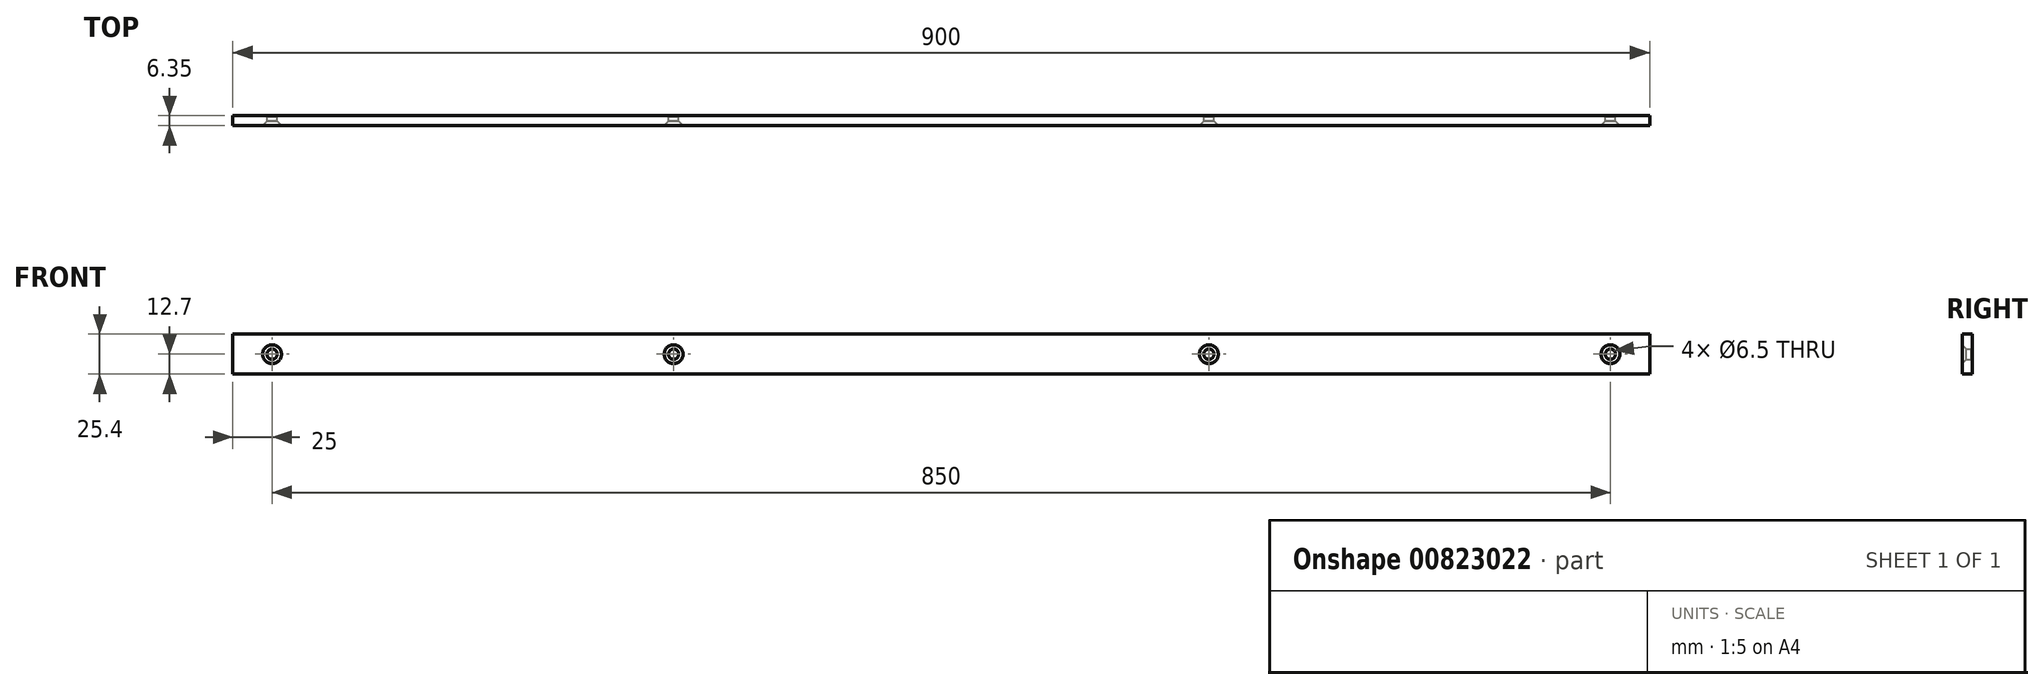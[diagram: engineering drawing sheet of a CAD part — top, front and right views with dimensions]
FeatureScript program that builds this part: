
annotation { "Feature Type Name" : "Feature", "Feature Type Description" : "" }
export const myFeature = defineFeature(function(context is Context, id is Id, definition is map)
    precondition{}
    {
        {
            var Q0;
            Q0=qCreatedBy(makeId("Front.planeOp"),FACE);
            var sketch = newSketch(context, id + "F0", { "sketchPlane" : qUnion([Q0])});
            skLineSegment(sketch, "E0.bottom", {"start": v(450, -12.7) * mm, "end": v(-450, -12.7) * mm});
            skLineSegment(sketch, "E0.top", {"start": v(450, 12.7) * mm, "end": v(-450, 12.7) * mm});
            skLineSegment(sketch, "E0.left", {"start": v(450, -12.7) * mm, "end": v(450, 12.7) * mm});
            skLineSegment(sketch, "E0.right", {"start": v(-450, -12.7) * mm, "end": v(-450, 12.7) * mm});
            skPoint(sketch, "E0.middle", {"position": v(0, 0) * mm});
            skLineSegment(sketch, "E1", {"start": v(0, 0) * mm, "end": v(0, -342.54) * mm, "construction": true});
            skLineSegment(sketch, "E2", {"start": v(0, 0) * mm, "end": v(-425, 0) * mm, "construction": true});
            skLineSegment(sketch, "E3", {"start": v(-425, 0) * mm, "end": v(-425, 337.75) * mm, "construction": true});
            skLineSegment(sketch, "E4", {"start": v(-425, 337.75) * mm, "end": v(-170, 337.75) * mm, "construction": true});
            skLineSegment(sketch, "E5", {"start": v(-170, 337.75) * mm, "end": v(-170, 0) * mm, "construction": true});
            skCircle(sketch, "E6", {"center": v(-425, 0) * mm, "radius": 3.25 * mm});
            skCircle(sketch, "E7", {"center": v(-170, 0) * mm, "radius": 3.25 * mm});
            skCircle(sketch, "E8.MirrorC", {"center": v(170, 0) * mm, "radius": 3.25 * mm});
            skCircle(sketch, "E9.MirrorC", {"center": v(425, 0) * mm, "radius": 3.25 * mm});
            skCircle(sketch, "E10", {"center": v(0, 0) * mm, "radius": 3.25 * mm, "construction": true});
            skSolve(sketch);
        }
        {
            var Q0;
            Q0 = qSketchRegion(id + "F0", true);
            extrude(context, id + "F1", {"entities" : qUnion([Q0]), "depth" : 6.35 * mm, "offsetDistance" : 25 * mm});
        }
        {
            var Q0;
            Q0=makeQuery(id+"F1.opExtrude","CAP_EDGE",EDGE,{"disambiguationData":[OSD([sQuery(id+"F0.wireOp",EDGE,"E6")])],"isStart":false});
            var Q1;
            Q1=makeQuery(id+"F1.opExtrude","CAP_EDGE",EDGE,{"disambiguationData":[OSD([sQuery(id+"F0.wireOp",EDGE,"E7")])],"isStart":false});
            var Q2;
            Q2=makeQuery(id+"F1.opExtrude","CAP_EDGE",EDGE,{"disambiguationData":[OSD([sQuery(id+"F0.wireOp",EDGE,"E10")])],"isStart":false});
            var Q3;
            Q3=makeQuery(id+"F1.opExtrude","CAP_EDGE",EDGE,{"disambiguationData":[OSD([sQuery(id+"F0.wireOp",EDGE,"E8.MirrorC")])],"isStart":false});
            var Q4;
            Q4=makeQuery(id+"F1.opExtrude","CAP_EDGE",EDGE,{"disambiguationData":[OSD([sQuery(id+"F0.wireOp",EDGE,"E9.MirrorC")])],"isStart":false});
            chamfer(context, id + "F2", {"entities" : qUnion([Q0, Q1, Q2, Q3, Q4]), "width" : 2.75 * mm, "tangentPropagation" : true});
        }
        {
            var Q0;
            Q0=makeQuery(id+"F1.opExtrude","CAP_EDGE",EDGE,{"disambiguationData":[OSD([sQuery(id+"F0.wireOp",EDGE,"E9.MirrorC")])],"isStart":true});
            var Q1;
            Q1=makeQuery(id+"F1.opExtrude","CAP_EDGE",EDGE,{"disambiguationData":[OSD([sQuery(id+"F0.wireOp",EDGE,"E8.MirrorC")])],"isStart":true});
            var Q2;
            Q2=makeQuery(id+"F1.opExtrude","CAP_EDGE",EDGE,{"disambiguationData":[OSD([sQuery(id+"F0.wireOp",EDGE,"E10")])],"isStart":true});
            var Q3;
            Q3=makeQuery(id+"F1.opExtrude","CAP_EDGE",EDGE,{"disambiguationData":[OSD([sQuery(id+"F0.wireOp",EDGE,"E7")])],"isStart":true});
            var Q4;
            Q4=makeQuery(id+"F1.opExtrude","CAP_EDGE",EDGE,{"disambiguationData":[OSD([sQuery(id+"F0.wireOp",EDGE,"E6")])],"isStart":true});
            chamfer(context, id + "F3", {"entities" : qUnion([Q0, Q1, Q2, Q3, Q4]), "width" : 0.5 * mm, "tangentPropagation" : true});
        }
    });
